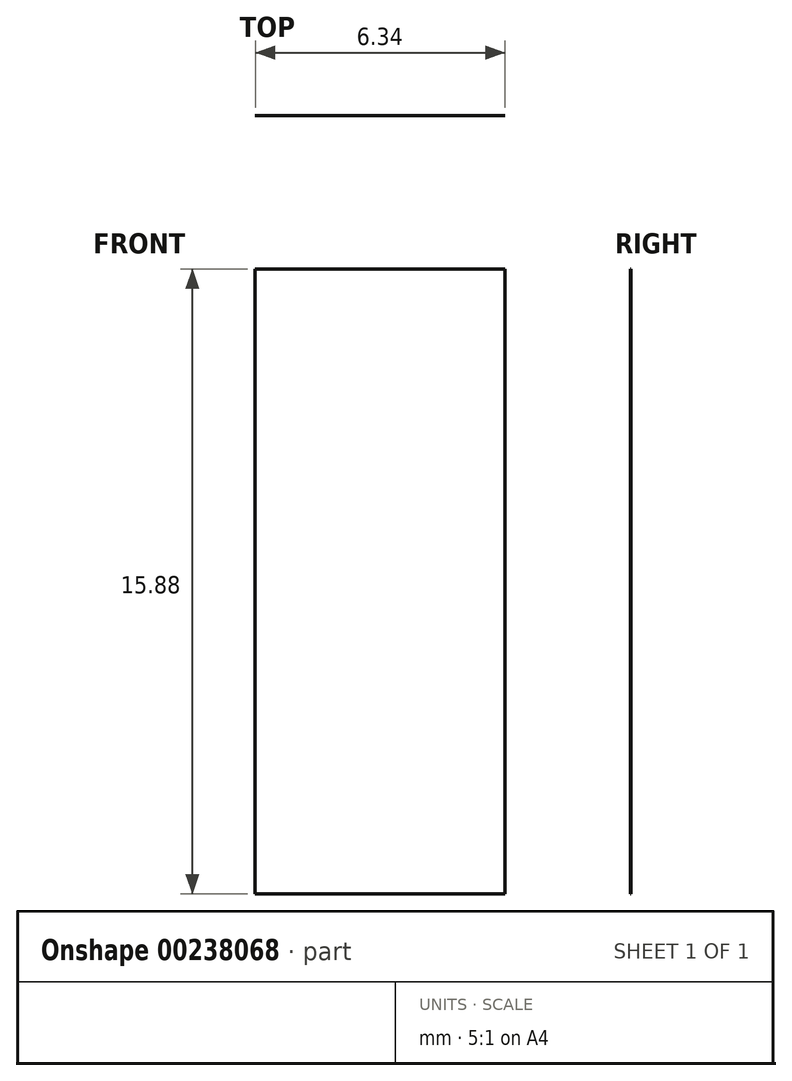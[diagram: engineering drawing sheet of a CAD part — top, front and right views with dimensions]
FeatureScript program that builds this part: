
annotation { "Feature Type Name" : "Feature", "Feature Type Description" : "" }
export const myFeature = defineFeature(function(context is Context, id is Id, definition is map)
    precondition{}
    {
        {
            var Q0;
            Q0=qCreatedBy(makeId("Front.planeOp"),FACE);
            var sketch = newSketch(context, id + "F0", { "sketchPlane" : qUnion([Q0])});
            skLineSegment(sketch, "E0.bottom", {"start": v(3.18, -7.94) * mm, "end": v(-3.17, -7.94) * mm});
            skLineSegment(sketch, "E0.top", {"start": v(3.17, 7.94) * mm, "end": v(-3.18, 7.94) * mm});
            skLineSegment(sketch, "E0.left", {"start": v(3.18, -7.94) * mm, "end": v(3.17, 7.94) * mm});
            skLineSegment(sketch, "E0.right", {"start": v(-3.17, -7.94) * mm, "end": v(-3.18, 7.94) * mm});
            skPoint(sketch, "E0.middle", {"position": v(0, 0) * mm});
            skSolve(sketch);
        }
        {
            var Q0;
            Q0 = qSketchRegion(id + "F0", true);
            extrude(context, id + "F1", {"entities" : qUnion([Q0]), "depth" : 1 / 203.2 * mm});
        }
    });
